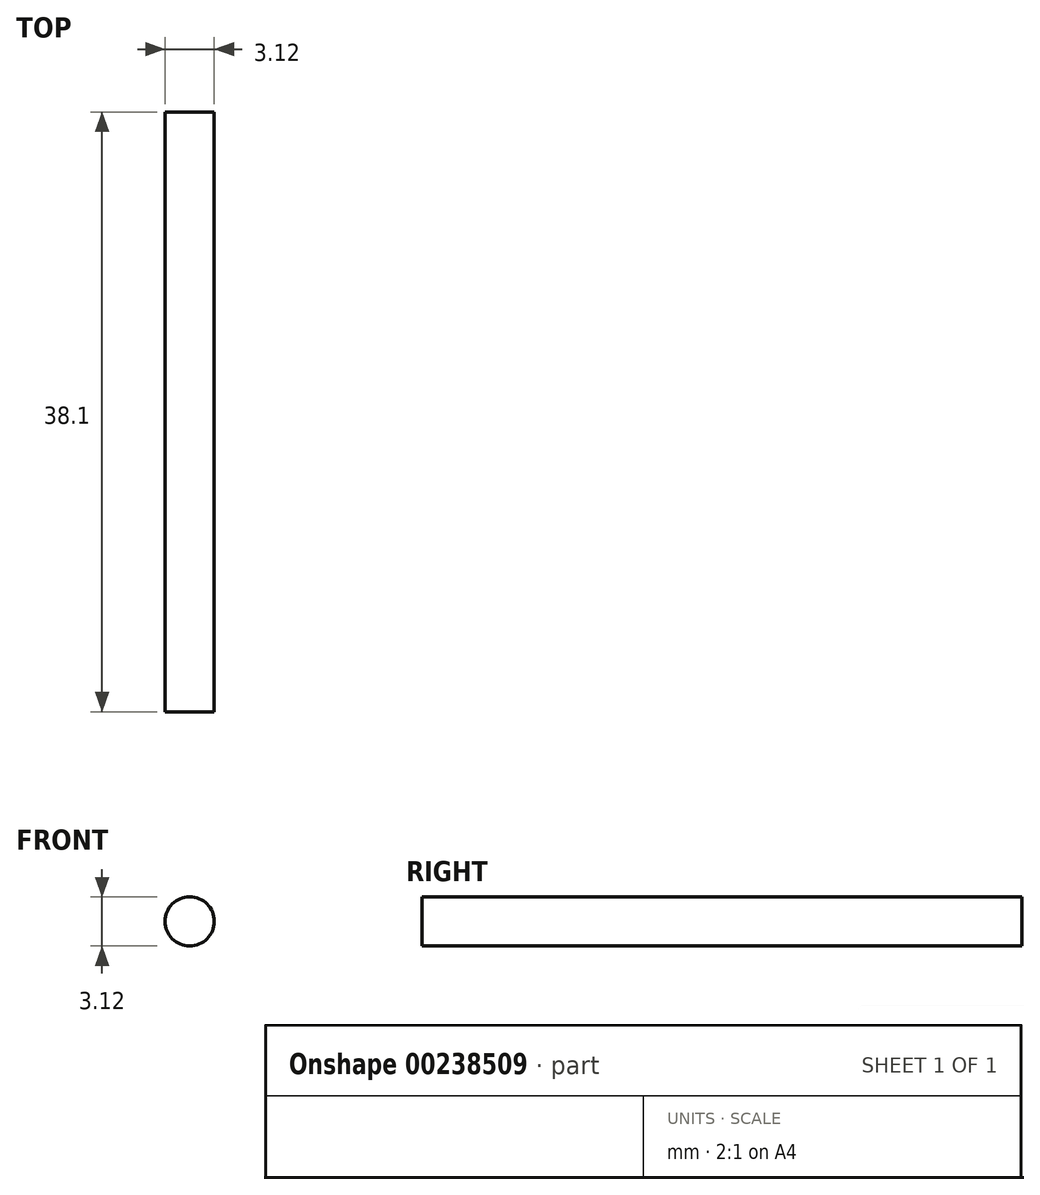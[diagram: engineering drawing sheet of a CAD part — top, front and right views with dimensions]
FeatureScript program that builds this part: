
annotation { "Feature Type Name" : "Feature", "Feature Type Description" : "" }
export const myFeature = defineFeature(function(context is Context, id is Id, definition is map)
    precondition{}
    {
        {
            var Q0;
            Q0=qCreatedBy(makeId("Front.planeOp"),FACE);
            var sketch = newSketch(context, id + "F0", { "sketchPlane" : qUnion([Q0])});
            skCircle(sketch, "E0", {"center": v(0, 0) * mm, "radius": 1.56 * mm});
            skSolve(sketch);
        }
        {
            var Q0;
            Q0=makeQuery(id+"F0.imprint","IMPRINT",FACE,{"disambiguationData":[TD([[makeQuery(id+"F0.imprint","IMPRINT",EDGE,{"derivedFrom":sQuery(id+"F0.wireOp",EDGE,"E0")}),1.0]])]});
            extrude(context, id + "F1", {"entities" : qUnion([Q0]), "depth" : 38.1 * mm});
        }
    });
